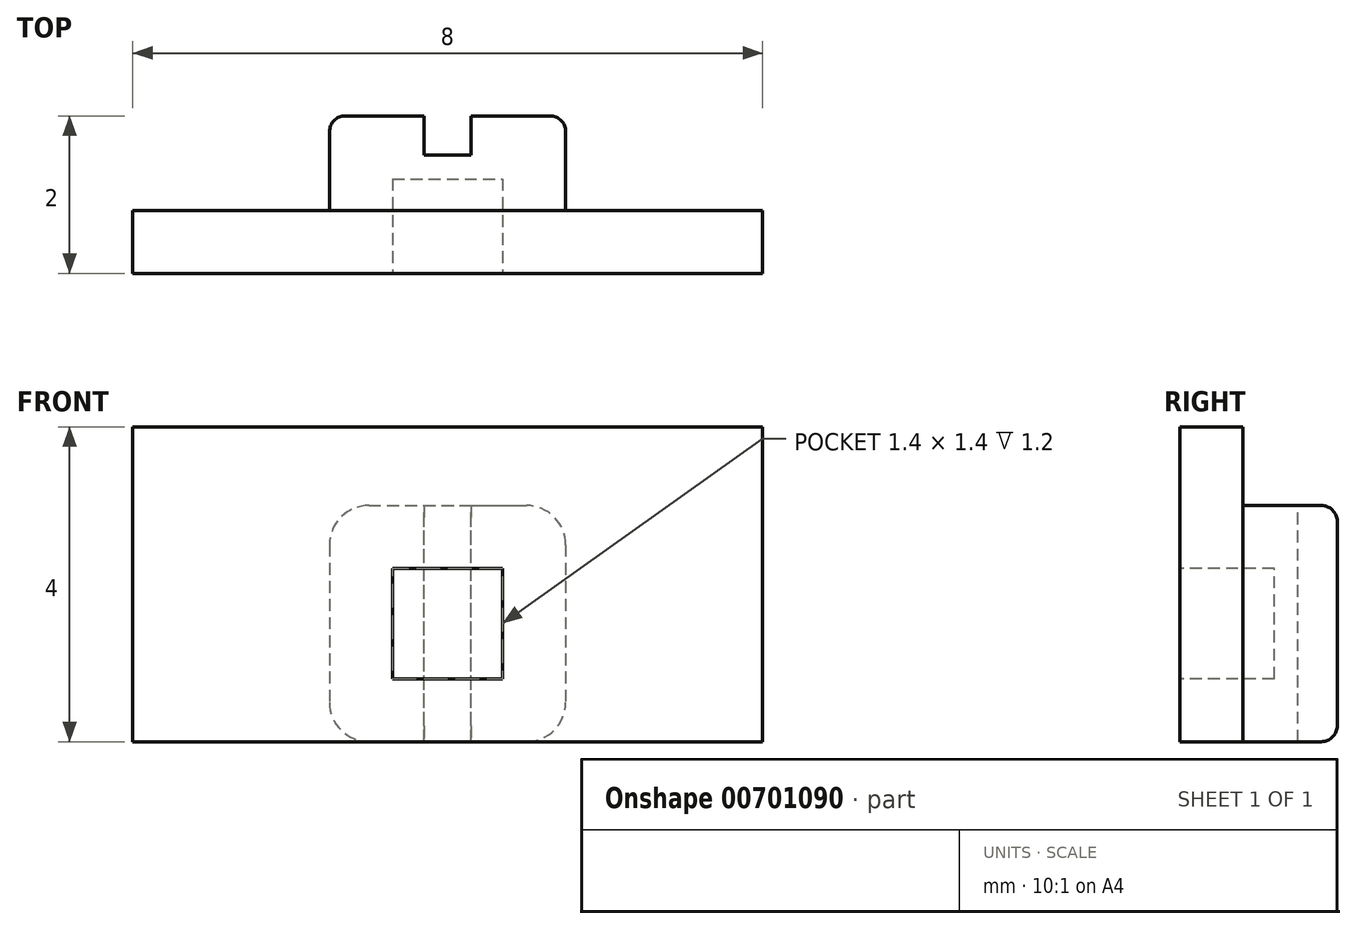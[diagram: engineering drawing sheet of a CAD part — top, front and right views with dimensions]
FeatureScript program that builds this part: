
annotation { "Feature Type Name" : "Feature", "Feature Type Description" : "" }
export const myFeature = defineFeature(function(context is Context, id is Id, definition is map)
    precondition{}
    {
        {
            var Q0;
            Q0=qCreatedBy(makeId("Top.planeOp"),FACE);
            var sketch = newSketch(context, id + "F0", { "sketchPlane" : qUnion([Q0])});
            skLineSegment(sketch, "E0.bottom", {"start": v(0, 0) * mm, "end": v(8, 0) * mm});
            skLineSegment(sketch, "E0.top", {"start": v(0, 0.8) * mm, "end": v(2.5, 0.8) * mm});
            skLineSegment(sketch, "E0.left", {"start": v(0, 0) * mm, "end": v(0, 0.8) * mm});
            skLineSegment(sketch, "E0.right", {"start": v(8, 0) * mm, "end": v(8, 0.8) * mm});
            skLineSegment(sketch, "E1", {"start": v(2.5, 0.8) * mm, "end": v(2.5, 2) * mm});
            skLineSegment(sketch, "E2", {"start": v(2.5, 2) * mm, "end": v(5.5, 2) * mm});
            skLineSegment(sketch, "E3", {"start": v(5.5, 2) * mm, "end": v(5.5, 0.8) * mm});
            skLineSegment(sketch, "E4.trimOffspring", {"start": v(5.5, 0.8) * mm, "end": v(8, 0.8) * mm});
            skSolve(sketch);
        }
        {
            var Q0;
            Q0=qSketchRegion(id+"F0",true);
            extrude(context, id + "F1", {"entities" : qUnion([Q0]), "depth" : 3 * mm, "offsetDistance" : 25 * mm});
        }
        {
            var Q0;
            Q0=makeQuery(id+"F1.opExtrude","SWEPT_FACE",FACE,{"disambiguationData":[OSD([sQuery(id+"F0.wireOp",EDGE,"E0.bottom")])]});
            var sketch = newSketch(context, id + "F2", { "sketchPlane" : qUnion([Q0])});
            skLineSegment(sketch, "E5.bottom", {"start": v(3.3, 0.8) * mm, "end": v(4.7, 0.8) * mm});
            skLineSegment(sketch, "E5.top", {"start": v(3.3, 2.2) * mm, "end": v(4.7, 2.2) * mm});
            skLineSegment(sketch, "E5.left", {"start": v(3.3, 0.8) * mm, "end": v(3.3, 2.2) * mm});
            skLineSegment(sketch, "E5.right", {"start": v(4.7, 0.8) * mm, "end": v(4.7, 2.2) * mm});
            skLineSegment(sketch, "E6", {"start": v(0, 1.5) * mm, "end": v(1.82, 1.5) * mm, "construction": true});
            skLineSegment(sketch, "E7", {"start": v(4, 0) * mm, "end": v(4, 0.82) * mm, "construction": true});
            skSolve(sketch);
        }
        {
            var Q0;
            Q0=qSketchRegion(id+"F2",true);
            extrude(context, id + "F3", {"entities" : qUnion([Q0]), "operationType" : NewBodyOperationType.REMOVE, "oppositeDirection" : true, "depth" : 1.2 * mm, "offsetDistance" : 25 * mm});
        }
        {
            var Q0;
            Q0=makeQuery(id+"F1.opExtrude","CAP_EDGE",EDGE,{"disambiguationData":[OSD([sQuery(id+"F0.wireOp",EDGE,"E3")])],"isStart":false});
            var Q1;
            Q1=makeQuery(id+"F1.opExtrude","CAP_EDGE",EDGE,{"disambiguationData":[OSD([sQuery(id+"F0.wireOp",EDGE,"E1")])],"isStart":false});
            var Q2;
            Q2=makeQuery(id+"F1.opExtrude","CAP_EDGE",EDGE,{"disambiguationData":[OSD([sQuery(id+"F0.wireOp",EDGE,"E1")])],"isStart":true});
            var Q3;
            Q3=makeQuery(id+"F1.opExtrude","CAP_EDGE",EDGE,{"disambiguationData":[OSD([sQuery(id+"F0.wireOp",EDGE,"E3")])],"isStart":true});
            fillet(context, id + "F4", {"entities" : qUnion([Q0, Q1, Q2, Q3]), "radius" : 0.5 * mm, "tangentPropagation" : true, "allowEdgeOverflow" : false});
        }
        {
            var Q0;
            Q0=makeQuery(id+"F1.opExtrude","SWEPT_FACE",FACE,{"disambiguationData":[OSD([sQuery(id+"F0.wireOp",EDGE,"E0.right")])]});
            var sketch = newSketch(context, id + "F5", { "sketchPlane" : qUnion([Q0])});
            skLineSegment(sketch, "E8.bottom", {"start": v(0, 3) * mm, "end": v(0.8, 3) * mm});
            skLineSegment(sketch, "E8.top", {"start": v(0, 4) * mm, "end": v(0.8, 4) * mm});
            skLineSegment(sketch, "E8.left", {"start": v(0, 3) * mm, "end": v(0, 4) * mm});
            skLineSegment(sketch, "E8.right", {"start": v(0.8, 3) * mm, "end": v(0.8, 4) * mm});
            skSolve(sketch);
        }
        {
            var Q0;
            Q0 = qSketchRegion(id + "F5", true);
            var Q1;
            Q1=makeQuery(id+"F1.opExtrude","SWEPT_FACE",FACE,{"disambiguationData":[OSD([sQuery(id+"F0.wireOp",EDGE,"E0.left")])]});
            extrude(context, id + "F6", {"entities" : qUnion([Q0]), "operationType" : NewBodyOperationType.ADD, "endBound" : BoundingType.UP_TO_SURFACE, "oppositeDirection" : true, "depth" : 25 * mm, "endBoundEntityFace" : qUnion([Q1]), "offsetDistance" : 25 * mm});
        }
        {
            var Q0;
            Q0=makeQuery(id+"F1.opExtrude","CAP_FACE",FACE,{"disambiguationData":[OSD([sQuery(id+"F0.wireOp",EDGE,"E0.bottom"),sQuery(id+"F0.wireOp",EDGE,"E0.top"),sQuery(id+"F0.wireOp",EDGE,"E0.left"),sQuery(id+"F0.wireOp",EDGE,"E0.right"),sQuery(id+"F0.wireOp",EDGE,"E1"),sQuery(id+"F0.wireOp",EDGE,"E2"),sQuery(id+"F0.wireOp",EDGE,"E3"),sQuery(id+"F0.wireOp",EDGE,"E4.trimOffspring")])],"isStart":false});
            var sketch = newSketch(context, id + "F7", { "sketchPlane" : qUnion([Q0])});
            skLineSegment(sketch, "E9.bottom", {"start": v(3.7, 2) * mm, "end": v(4.3, 2) * mm});
            skLineSegment(sketch, "E9.top", {"start": v(3.7, 1.5) * mm, "end": v(4.3, 1.5) * mm});
            skLineSegment(sketch, "E9.left", {"start": v(3.7, 2) * mm, "end": v(3.7, 1.5) * mm});
            skLineSegment(sketch, "E9.right", {"start": v(4.3, 2) * mm, "end": v(4.3, 1.5) * mm});
            skLineSegment(sketch, "E10", {"start": v(4, 0.43) * mm, "end": v(4, 2) * mm, "construction": true});
            skPoint(sketch, "E10.startSnap0", {"position": v(4, 2) * mm});
            skSolve(sketch);
        }
        {
            var Q0;
            Q0 = qSketchRegion(id + "F7", true);
            extrude(context, id + "F8", {"entities" : qUnion([Q0]), "operationType" : NewBodyOperationType.REMOVE, "endBound" : BoundingType.UP_TO_NEXT, "oppositeDirection" : true, "depth" : 25 * mm, "offsetDistance" : 25 * mm});
        }
        {
            var Q0;
            Q0=makeQuery(id+"F1.opExtrude","CAP_EDGE",EDGE,{"disambiguationData":[OSD([sQuery(id+"F0.wireOp",EDGE,"E2")])],"isStart":false});
            var Q1;
            Q1=makeQuery(id+"F4.opFillet","BLEND_EDGE",EDGE,{"blendedFrom":[makeQuery(id+"F1.opExtrude","CAP_EDGE",EDGE,{"disambiguationData":[OSD([sQuery(id+"F0.wireOp",EDGE,"E3")])],"isStart":false}),makeQuery(id+"F1.opExtrude","SWEPT_FACE",FACE,{"disambiguationData":[OSD([sQuery(id+"F0.wireOp",EDGE,"E2")])]})],"blendedInto":[makeQuery(id+"F1.opExtrude","SWEPT_FACE",FACE,{"disambiguationData":[OSD([sQuery(id+"F0.wireOp",EDGE,"E2")])]})]});
            var Q2;
            Q2=makeQuery(id+"F1.opExtrude","SWEPT_EDGE",EDGE,{"disambiguationData":[OSD([sQuery(id+"F0.wireOp",EDGE,"E2"),sQuery(id+"F0.wireOp",EDGE,"E3")])]});
            var Q3;
            Q3=makeQuery(id+"F4.opFillet","BLEND_EDGE",EDGE,{"blendedFrom":[makeQuery(id+"F1.opExtrude","CAP_EDGE",EDGE,{"disambiguationData":[OSD([sQuery(id+"F0.wireOp",EDGE,"E3")])],"isStart":true}),makeQuery(id+"F1.opExtrude","SWEPT_FACE",FACE,{"disambiguationData":[OSD([sQuery(id+"F0.wireOp",EDGE,"E2")])]})],"blendedInto":[makeQuery(id+"F1.opExtrude","SWEPT_FACE",FACE,{"disambiguationData":[OSD([sQuery(id+"F0.wireOp",EDGE,"E2")])]})]});
            var Q4;
            Q4=makeQuery(id+"F1.opExtrude","CAP_EDGE",EDGE,{"disambiguationData":[OSD([sQuery(id+"F0.wireOp",EDGE,"E2")])],"isStart":true});
            var Q5;
            Q5=makeQuery(id+"F4.opFillet","BLEND_EDGE",EDGE,{"blendedFrom":[makeQuery(id+"F1.opExtrude","CAP_EDGE",EDGE,{"disambiguationData":[OSD([sQuery(id+"F0.wireOp",EDGE,"E1")])],"isStart":true}),makeQuery(id+"F1.opExtrude","SWEPT_FACE",FACE,{"disambiguationData":[OSD([sQuery(id+"F0.wireOp",EDGE,"E2")])]})],"blendedInto":[makeQuery(id+"F1.opExtrude","SWEPT_FACE",FACE,{"disambiguationData":[OSD([sQuery(id+"F0.wireOp",EDGE,"E2")])]})]});
            var Q6;
            Q6=makeQuery(id+"F1.opExtrude","SWEPT_EDGE",EDGE,{"disambiguationData":[OSD([sQuery(id+"F0.wireOp",EDGE,"E1"),sQuery(id+"F0.wireOp",EDGE,"E2")])]});
            var Q7;
            Q7=makeQuery(id+"F4.opFillet","BLEND_EDGE",EDGE,{"blendedFrom":[makeQuery(id+"F1.opExtrude","CAP_EDGE",EDGE,{"disambiguationData":[OSD([sQuery(id+"F0.wireOp",EDGE,"E1")])],"isStart":false}),makeQuery(id+"F1.opExtrude","SWEPT_FACE",FACE,{"disambiguationData":[OSD([sQuery(id+"F0.wireOp",EDGE,"E2")])]})],"blendedInto":[makeQuery(id+"F1.opExtrude","SWEPT_FACE",FACE,{"disambiguationData":[OSD([sQuery(id+"F0.wireOp",EDGE,"E2")])]})]});
            fillet(context, id + "F9", {"entities" : qUnion([Q0, Q1, Q2, Q3, Q4, Q5, Q6, Q7]), "radius" : 0.2 * mm, "tangentPropagation" : true, "allowEdgeOverflow" : false});
        }
    });
